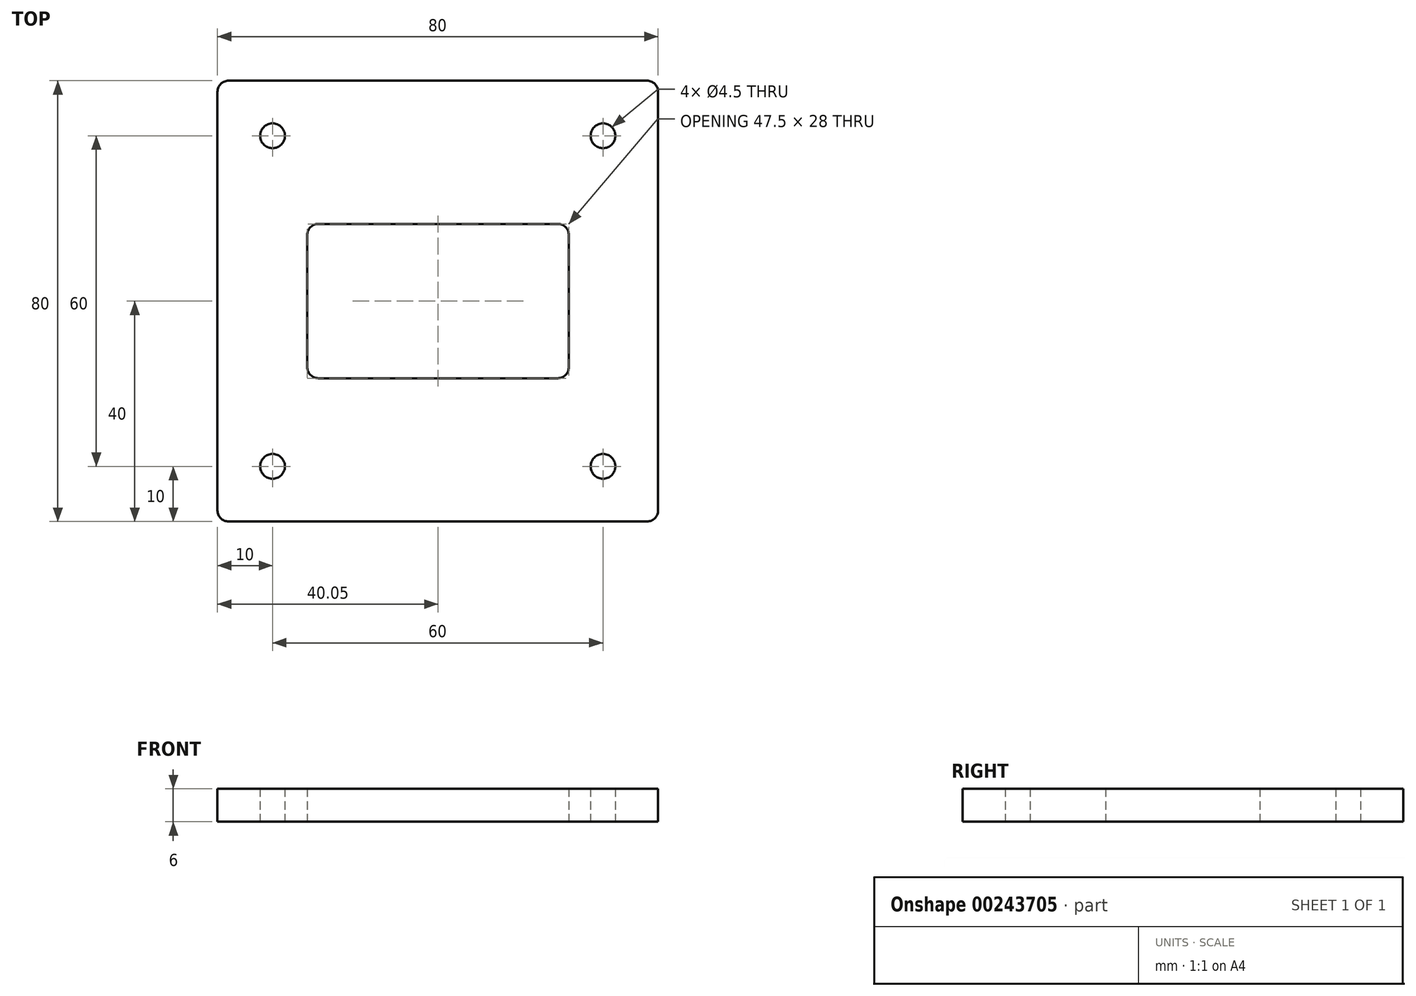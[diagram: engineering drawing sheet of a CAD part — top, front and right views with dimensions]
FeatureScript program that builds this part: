
annotation { "Feature Type Name" : "Feature", "Feature Type Description" : "" }
export const myFeature = defineFeature(function(context is Context, id is Id, definition is map)
    precondition{}
    {
        {
            var Q0;
            Q0=qCreatedBy(makeId("Top.planeOp"),FACE);
            var sketch = newSketch(context, id + "F0", { "sketchPlane" : qUnion([Q0])});
            skLineSegment(sketch, "E0.bottom", {"start": v(2, 0) * mm, "end": v(45.5, 0) * mm});
            skLineSegment(sketch, "E0.top", {"start": v(2, 28) * mm, "end": v(45.5, 28) * mm});
            skLineSegment(sketch, "E0.left", {"start": v(0, 2) * mm, "end": v(0, 26) * mm});
            skLineSegment(sketch, "E0.right", {"start": v(47.5, 2) * mm, "end": v(47.5, 26) * mm});
            skLineSegment(sketch, "E1.bottom", {"start": v(-14.3, 54) * mm, "end": v(61.7, 54) * mm});
            skLineSegment(sketch, "E1.top", {"start": v(-14.3, -26) * mm, "end": v(61.7, -26) * mm});
            skLineSegment(sketch, "E1.left", {"start": v(-16.3, 52) * mm, "end": v(-16.3, -24) * mm});
            skLineSegment(sketch, "E1.right", {"start": v(63.7, 52) * mm, "end": v(63.7, -24) * mm});
            skCircle(sketch, "E2", {"center": v(-6.3, 44) * mm, "radius": 2.25 * mm});
            skCircle(sketch, "E3", {"center": v(53.7, 44) * mm, "radius": 2.25 * mm});
            skCircle(sketch, "E4", {"center": v(-6.3, -16) * mm, "radius": 2.25 * mm});
            skCircle(sketch, "E5", {"center": v(53.7, -16) * mm, "radius": 2.25 * mm});
            skPoint(sketch, "E6.visualSharp", {"position": v(47.5, 28) * mm});
            skArc(sketch, "E6.filletArc", {"start": v(47.5, 26) * mm, "mid": v(46.91, 27.41) * mm, "end": v(45.5, 28) * mm});
            skPoint(sketch, "E7.visualSharp", {"position": v(47.5, 0) * mm});
            skArc(sketch, "E7.filletArc", {"start": v(45.5, 0) * mm, "mid": v(46.91, 0.59) * mm, "end": v(47.5, 2) * mm});
            skPoint(sketch, "E8.visualSharp", {"position": v(0, 0) * mm});
            skArc(sketch, "E8.filletArc", {"start": v(0, 2) * mm, "mid": v(0.59, 0.59) * mm, "end": v(2, 0) * mm});
            skPoint(sketch, "E9.visualSharp", {"position": v(0, 28) * mm});
            skArc(sketch, "E9.filletArc", {"start": v(2, 28) * mm, "mid": v(0.59, 27.41) * mm, "end": v(0, 26) * mm});
            skPoint(sketch, "E10.visualSharp", {"position": v(63.7, -26) * mm});
            skArc(sketch, "E10.filletArc", {"start": v(61.7, -26) * mm, "mid": v(63.11, -25.41) * mm, "end": v(63.7, -24) * mm});
            skPoint(sketch, "E11.visualSharp", {"position": v(-16.3, -26) * mm});
            skArc(sketch, "E11.filletArc", {"start": v(-16.3, -24) * mm, "mid": v(-15.71, -25.41) * mm, "end": v(-14.3, -26) * mm});
            skPoint(sketch, "E12.visualSharp", {"position": v(-16.3, 54) * mm});
            skArc(sketch, "E12.filletArc", {"start": v(-14.3, 54) * mm, "mid": v(-15.71, 53.41) * mm, "end": v(-16.3, 52) * mm});
            skPoint(sketch, "E13.visualSharp", {"position": v(63.7, 54) * mm});
            skArc(sketch, "E13.filletArc", {"start": v(63.7, 52) * mm, "mid": v(63.11, 53.41) * mm, "end": v(61.7, 54) * mm});
            skSolve(sketch);
        }
        {
            var Q0;
            Q0 = qSketchRegion(id + "F0", true);
            extrude(context, id + "F1", {"entities" : qUnion([Q0]), "depth" : 6 * mm});
        }
    });
